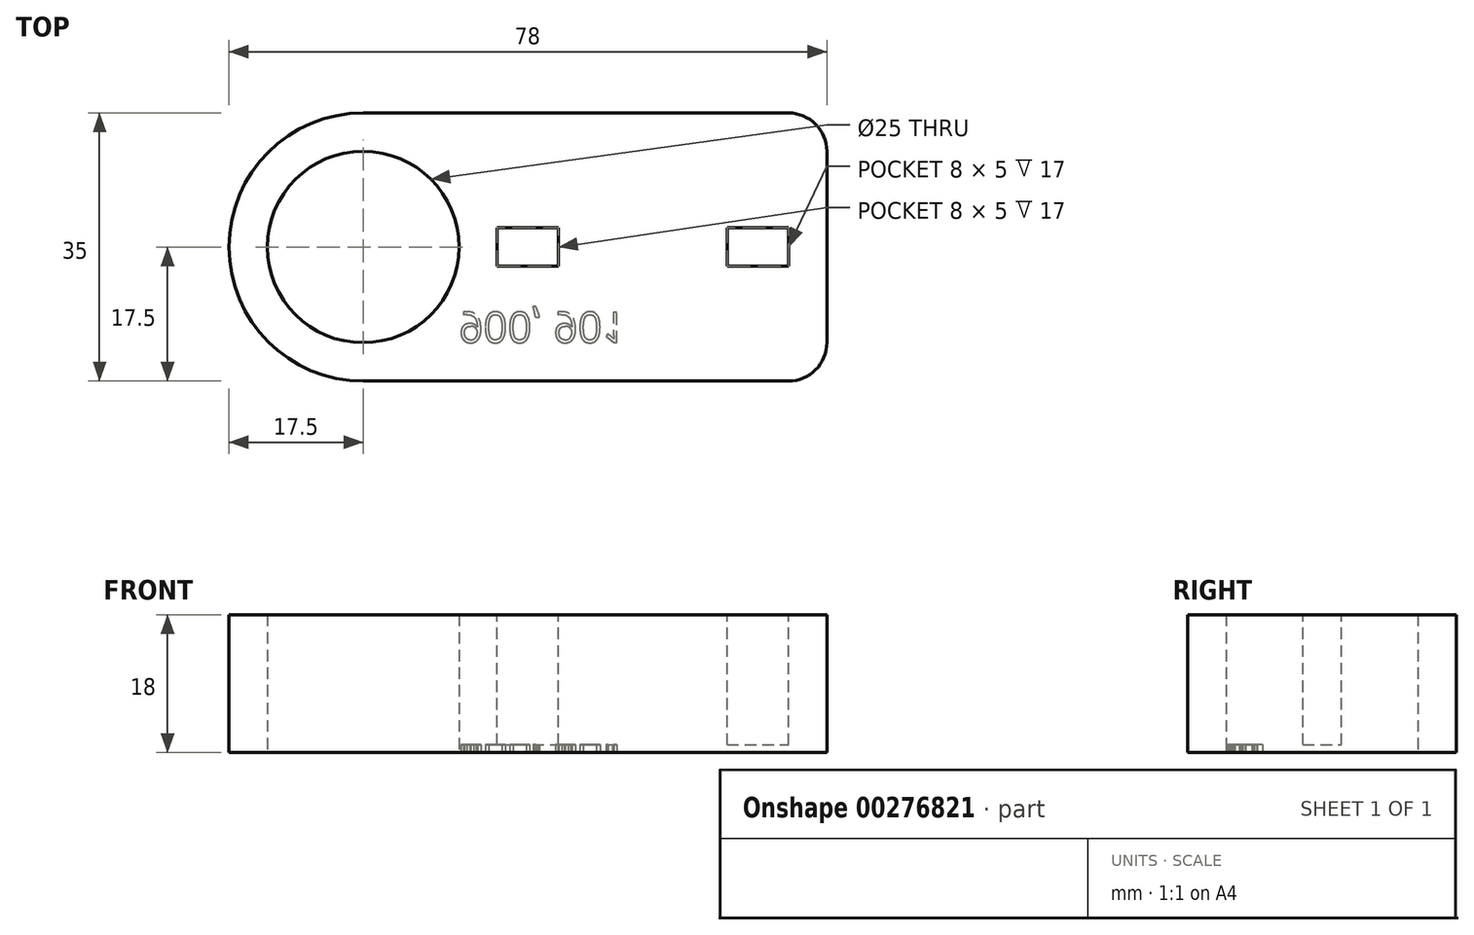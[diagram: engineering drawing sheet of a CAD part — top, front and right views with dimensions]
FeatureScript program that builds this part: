
annotation { "Feature Type Name" : "Feature", "Feature Type Description" : "" }
export const myFeature = defineFeature(function(context is Context, id is Id, definition is map)
    precondition{}
    {
        {
            var Q0;
            Q0=qCreatedBy(makeId("Top.planeOp"),FACE);
            var sketch = newSketch(context, id + "F0", { "sketchPlane" : qUnion([Q0])});
            skLineSegment(sketch, "E0.bottom", {"start": v(17.5, 0) * mm, "end": v(73, 0) * mm});
            skLineSegment(sketch, "E0.top", {"start": v(17.5, 35) * mm, "end": v(73, 35) * mm});
            skLineSegment(sketch, "E0.left", {"start": v(0, 17.5) * mm, "end": v(0, 17.5) * mm});
            skLineSegment(sketch, "E0.right", {"start": v(78, 5) * mm, "end": v(78, 30) * mm});
            skLineSegment(sketch, "E1.bottom", {"start": v(0, 0) * mm, "end": v(17.5, 0) * mm, "construction": true});
            skLineSegment(sketch, "E1.top", {"start": v(0, 17.5) * mm, "end": v(17.5, 17.5) * mm, "construction": true});
            skLineSegment(sketch, "E1.left", {"start": v(0, 0) * mm, "end": v(0, 17.5) * mm, "construction": true});
            skLineSegment(sketch, "E1.right", {"start": v(17.5, 0) * mm, "end": v(17.5, 17.5) * mm, "construction": true});
            skCircle(sketch, "E2", {"center": v(17.5, 17.5) * mm, "radius": 12.5 * mm});
            skPoint(sketch, "E3.visualSharp", {"position": v(0, 0) * mm});
            skArc(sketch, "E3.filletArc", {"start": v(0, 17.5) * mm, "mid": v(5.13, 5.13) * mm, "end": v(17.5, 0) * mm});
            skPoint(sketch, "E4.visualSharp", {"position": v(0, 35) * mm});
            skArc(sketch, "E4.filletArc", {"start": v(17.5, 35) * mm, "mid": v(5.13, 29.87) * mm, "end": v(0, 17.5) * mm});
            skPoint(sketch, "E5.visualSharp", {"position": v(78, 35) * mm});
            skArc(sketch, "E5.filletArc", {"start": v(78, 30) * mm, "mid": v(76.54, 33.54) * mm, "end": v(73, 35) * mm});
            skPoint(sketch, "E6.visualSharp", {"position": v(78, 0) * mm});
            skArc(sketch, "E6.filletArc", {"start": v(73, 0) * mm, "mid": v(76.54, 1.46) * mm, "end": v(78, 5) * mm});
            skSolve(sketch);
        }
        {
            var Q0;
            Q0=makeQuery(id+"F0.imprint","IMPRINT",FACE,{"disambiguationData":[TD([[makeQuery(id+"F0.imprint","IMPRINT",EDGE,{"derivedFrom":sQuery(id+"F0.wireOp",EDGE,"E0.bottom")}),1.0]])]});
            extrude(context, id + "F1", {"entities" : qUnion([Q0]), "depth" : 18 * mm});
        }
        {
            var Q0;
            Q0=makeQuery(id+"F1.opExtrude","CAP_FACE",FACE,{"disambiguationData":[OSD([sQuery(id+"F0.wireOp",EDGE,"E0.bottom"),sQuery(id+"F0.wireOp",EDGE,"E0.top"),sQuery(id+"F0.wireOp",EDGE,"E0.right"),sQuery(id+"F0.wireOp",EDGE,"E2"),sQuery(id+"F0.wireOp",EDGE,"E3.filletArc"),sQuery(id+"F0.wireOp",EDGE,"E4.filletArc"),sQuery(id+"F0.wireOp",EDGE,"E5.filletArc"),sQuery(id+"F0.wireOp",EDGE,"E6.filletArc")])],"isStart":false});
            var sketch = newSketch(context, id + "F2", { "sketchPlane" : qUnion([Q0])});
            skLineSegment(sketch, "E7.bottom", {"start": v(0, 0) * mm, "end": v(35, 0) * mm, "construction": true});
            skLineSegment(sketch, "E7.top", {"start": v(0, 15) * mm, "end": v(35, 15) * mm, "construction": true});
            skLineSegment(sketch, "E7.left", {"start": v(0, 0) * mm, "end": v(0, 15) * mm, "construction": true});
            skLineSegment(sketch, "E7.right", {"start": v(35, 0) * mm, "end": v(35, 15) * mm, "construction": true});
            skLineSegment(sketch, "E8.bottom", {"start": v(35, 15) * mm, "end": v(43, 15) * mm});
            skLineSegment(sketch, "E8.top", {"start": v(35, 20) * mm, "end": v(43, 20) * mm});
            skLineSegment(sketch, "E8.left", {"start": v(35, 15) * mm, "end": v(35, 20) * mm});
            skLineSegment(sketch, "E8.right", {"start": v(43, 15) * mm, "end": v(43, 20) * mm});
            skLineSegment(sketch, "E9", {"start": v(43, 15) * mm, "end": v(65, 15) * mm, "construction": true});
            skLineSegment(sketch, "E10.bottom", {"start": v(65, 15) * mm, "end": v(73, 15) * mm});
            skLineSegment(sketch, "E10.top", {"start": v(65, 20) * mm, "end": v(73, 20) * mm});
            skLineSegment(sketch, "E10.left", {"start": v(65, 15) * mm, "end": v(65, 20) * mm});
            skLineSegment(sketch, "E10.right", {"start": v(73, 15) * mm, "end": v(73, 20) * mm});
            skSolve(sketch);
        }
        {
            var Q0;
            Q0=qSketchRegion(id+"F2",true);
            extrude(context, id + "F3", {"entities" : qUnion([Q0]), "operationType" : NewBodyOperationType.REMOVE, "oppositeDirection" : true, "depth" : 17 * mm});
        }
        {
            var Q0;
            Q0=makeQuery(id+"F1.opExtrude","CAP_FACE",FACE,{"disambiguationData":[OSD([sQuery(id+"F0.wireOp",EDGE,"E0.bottom"),sQuery(id+"F0.wireOp",EDGE,"E0.top"),sQuery(id+"F0.wireOp",EDGE,"E0.right"),sQuery(id+"F0.wireOp",EDGE,"E2"),sQuery(id+"F0.wireOp",EDGE,"E3.filletArc"),sQuery(id+"F0.wireOp",EDGE,"E4.filletArc"),sQuery(id+"F0.wireOp",EDGE,"E5.filletArc"),sQuery(id+"F0.wireOp",EDGE,"E6.filletArc")])],"isStart":true});
            var sketch = newSketch(context, id + "F4", { "sketchPlane" : qUnion([Q0])});
            skLineSegment(sketch, "E11.bottom", {"start": v(0, 0) * mm, "end": v(30, 0) * mm, "construction": true});
            skLineSegment(sketch, "E11.top", {"start": v(0, -5) * mm, "end": v(30, -5) * mm, "construction": true});
            skLineSegment(sketch, "E11.left", {"start": v(0, 0) * mm, "end": v(0, -5) * mm, "construction": true});
            skLineSegment(sketch, "E11.right", {"start": v(30, 0) * mm, "end": v(30, -5) * mm, "construction": true});
            skText(sketch, "E12", { "text": "900, 901", "fontName": "OpenSans-Regular.ttf"});
            const initialGuessF4  = {"E12": [0.03, -0.009, 1, 0, 0.004]};
            skSetInitialGuess(sketch, initialGuessF4);
            skSolve(sketch);
        }
        {
            var Q0;
            Q0 = qSketchRegion(id + "F4", true);
            extrude(context, id + "F5", {"entities" : qUnion([Q0]), "operationType" : NewBodyOperationType.REMOVE, "oppositeDirection" : true, "depth" : 1 * mm});
        }
    });
